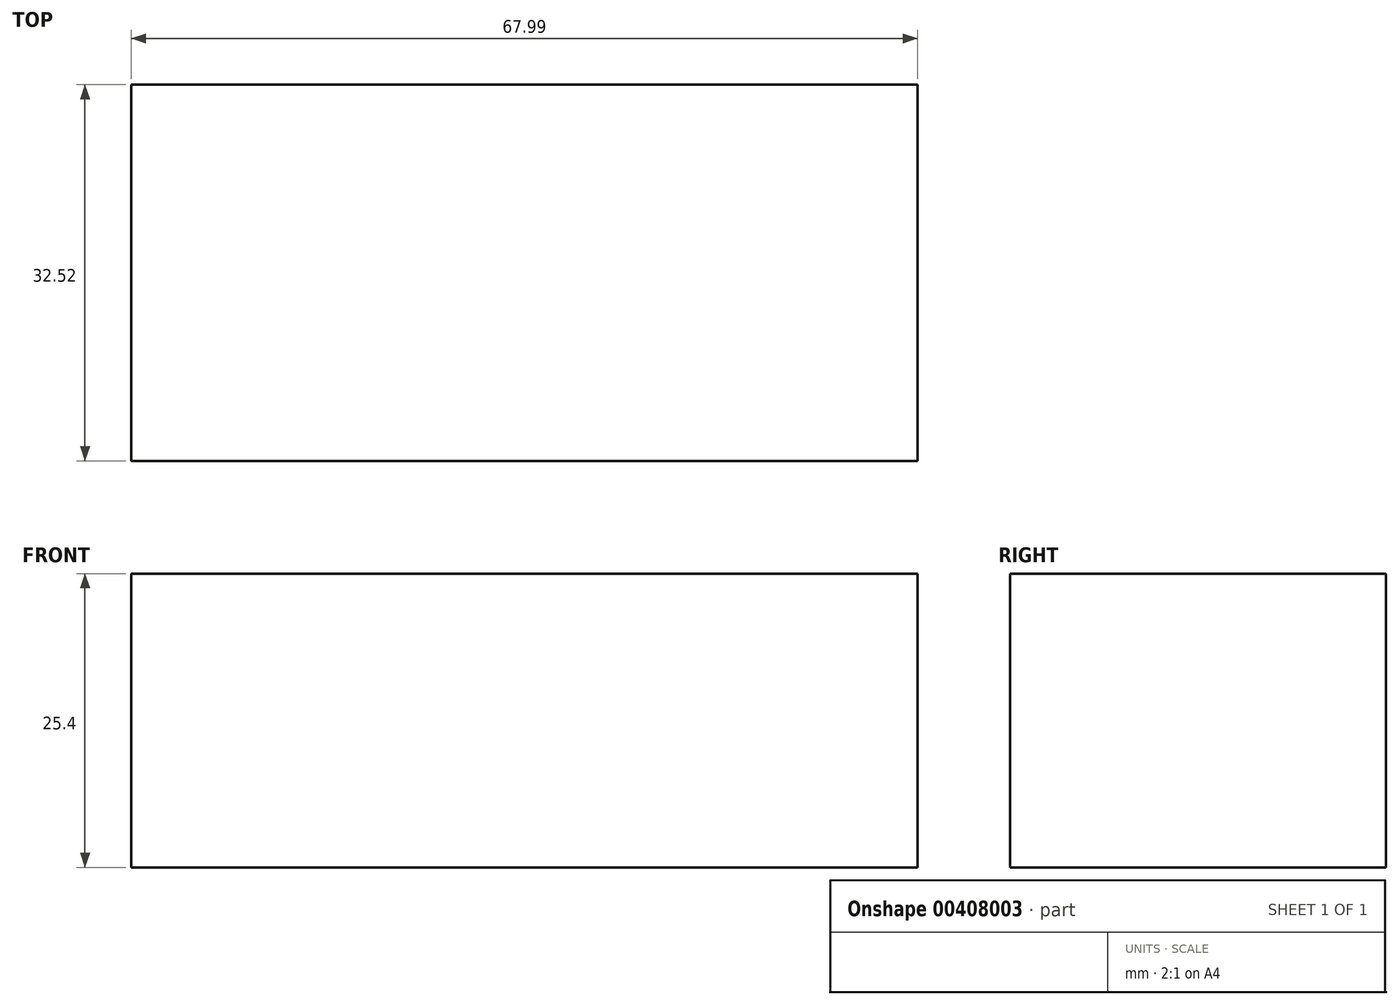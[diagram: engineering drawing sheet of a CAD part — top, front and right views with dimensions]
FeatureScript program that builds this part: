
annotation { "Feature Type Name" : "Feature", "Feature Type Description" : "" }
export const myFeature = defineFeature(function(context is Context, id is Id, definition is map)
    precondition{}
    {
        {
            var Q0;
            Q0=qCreatedBy(makeId("Top.planeOp"),FACE);
            var sketch = newSketch(context, id + "F0", { "sketchPlane" : qUnion([Q0])});
            skLineSegment(sketch, "E0", {"start": v(-38.82, 42.57) * mm, "end": v(29.17, 42.57) * mm});
            skLineSegment(sketch, "E1", {"start": v(29.17, 42.57) * mm, "end": v(29.17, 10.05) * mm});
            skLineSegment(sketch, "E2", {"start": v(-38.82, 42.57) * mm, "end": v(-38.82, 10.05) * mm});
            skLineSegment(sketch, "E3", {"start": v(29.17, 10.05) * mm, "end": v(-38.82, 10.05) * mm});
            skSolve(sketch);
        }
        {
            var Q0;
            Q0=sQuery(id+"F0.wireOp",EDGE,"E0");
            var Q1;
            Q1=sQuery(id+"F0.wireOp",EDGE,"E3");
            var Q2;
            Q2=sQuery(id+"F0.wireOp",EDGE,"E1");
            var Q3;
            Q3=sQuery(id+"F0.wireOp",EDGE,"E2");
            extrude(context, id + "F1", {"bodyType" : ToolBodyType.SURFACE, "surfaceEntities" : qUnion([Q0, Q1, Q2, Q3]), "depth" : 25.4 * mm});
        }
    });
